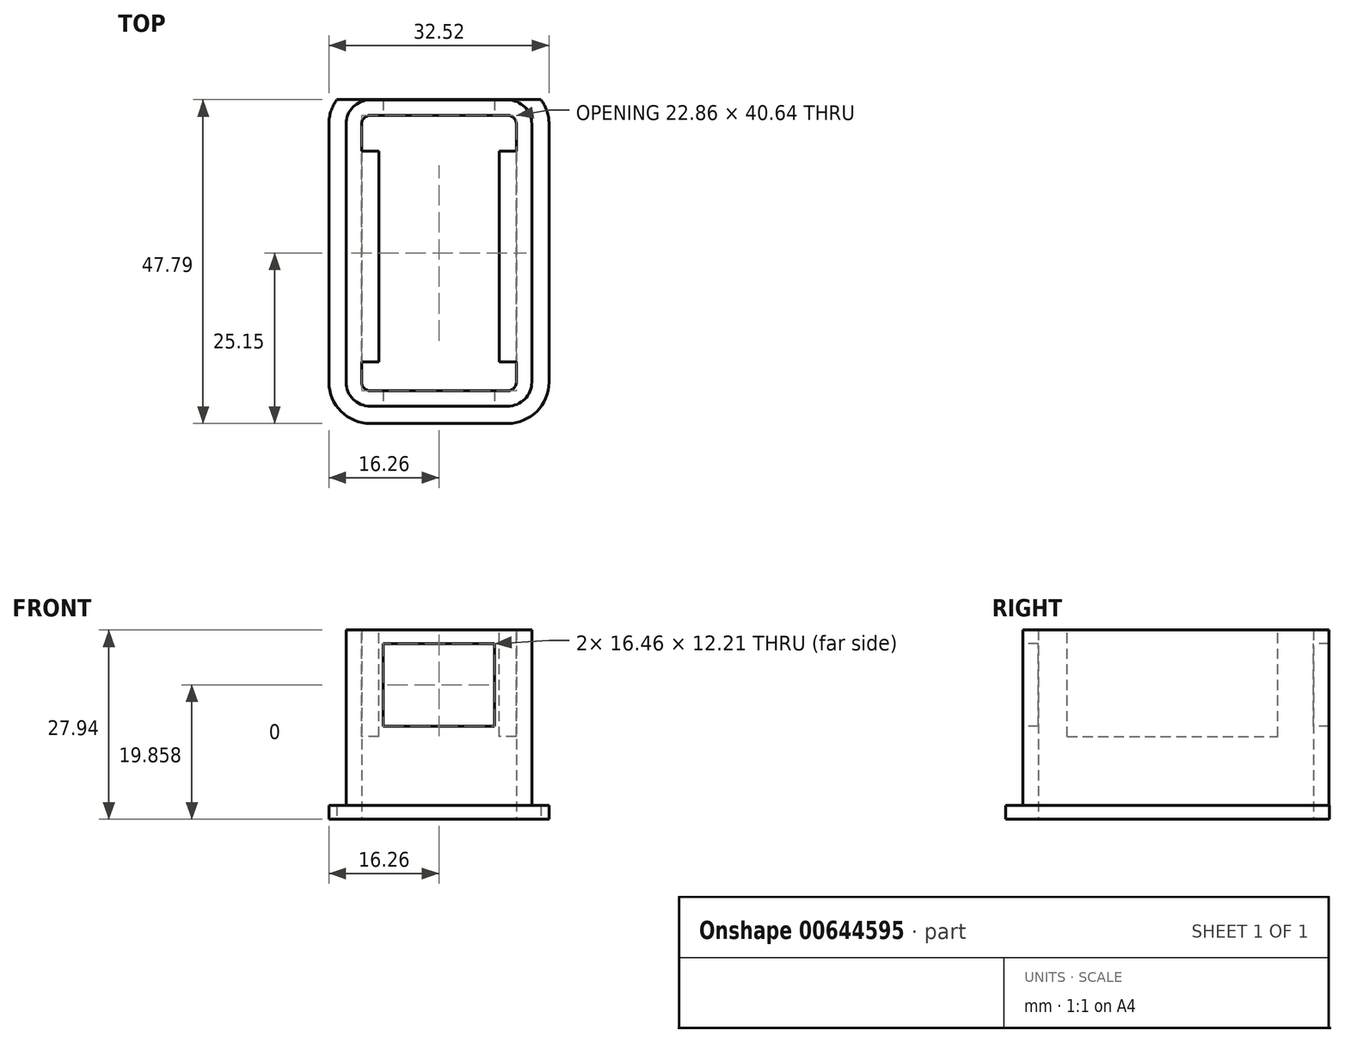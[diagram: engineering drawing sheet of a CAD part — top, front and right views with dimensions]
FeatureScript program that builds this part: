
annotation { "Feature Type Name" : "Feature", "Feature Type Description" : "" }
export const myFeature = defineFeature(function(context is Context, id is Id, definition is map)
    precondition{}
    {
        {
            var Q0;
            Q0=qCreatedBy(makeId("Top.planeOp"),FACE);
            var sketch = newSketch(context, id + "F0", { "sketchPlane" : qUnion([Q0])});
            skLineSegment(sketch, "E0.bottom", {"start": v(1.27, 0) * mm, "end": v(21.59, 0) * mm});
            skLineSegment(sketch, "E0.top", {"start": v(1.27, 40.64) * mm, "end": v(21.59, 40.64) * mm});
            skLineSegment(sketch, "E0.left", {"start": v(0, 1.27) * mm, "end": v(0, 39.37) * mm});
            skLineSegment(sketch, "E0.right", {"start": v(22.86, 1.27) * mm, "end": v(22.86, 39.37) * mm});
            skPoint(sketch, "E1.visualSharp", {"position": v(0, 40.64) * mm});
            skArc(sketch, "E1.filletArc", {"start": v(1.27, 40.64) * mm, "mid": v(0.37, 40.27) * mm, "end": v(0, 39.37) * mm});
            skPoint(sketch, "E2.visualSharp", {"position": v(22.86, 40.64) * mm});
            skArc(sketch, "E2.filletArc", {"start": v(22.86, 39.37) * mm, "mid": v(22.49, 40.27) * mm, "end": v(21.59, 40.64) * mm});
            skPoint(sketch, "E3.visualSharp", {"position": v(22.86, 0) * mm});
            skArc(sketch, "E3.filletArc", {"start": v(21.59, 0) * mm, "mid": v(22.49, 0.37) * mm, "end": v(22.86, 1.27) * mm});
            skPoint(sketch, "E4.visualSharp", {"position": v(0, 0) * mm});
            skArc(sketch, "E4.filletArc", {"start": v(0, 1.27) * mm, "mid": v(0.37, 0.37) * mm, "end": v(1.27, 0) * mm});
            skArc(sketch, "E5.0", {"start": v(-2.29, 1.27) * mm, "mid": v(-1.24, -1.24) * mm, "end": v(1.27, -2.29) * mm});
            skLineSegment(sketch, "E5.1", {"start": v(1.27, -2.29) * mm, "end": v(21.59, -2.29) * mm});
            skLineSegment(sketch, "E5.2", {"start": v(-2.29, 1.27) * mm, "end": v(-2.29, 39.37) * mm});
            skArc(sketch, "E5.3", {"start": v(21.59, -2.29) * mm, "mid": v(24.1, -1.24) * mm, "end": v(25.15, 1.27) * mm});
            skArc(sketch, "E5.4", {"start": v(1.27, 42.93) * mm, "mid": v(-1.24, 41.88) * mm, "end": v(-2.29, 39.37) * mm});
            skLineSegment(sketch, "E5.5", {"start": v(1.27, 42.93) * mm, "end": v(21.59, 42.93) * mm});
            skArc(sketch, "E5.6", {"start": v(25.15, 39.37) * mm, "mid": v(24.1, 41.88) * mm, "end": v(21.59, 42.93) * mm});
            skLineSegment(sketch, "E5.7", {"start": v(25.15, 1.27) * mm, "end": v(25.15, 39.37) * mm});
            skSolve(sketch);
        }
        {
            var Q0;
            Q0=makeQuery(id+"F0.imprint","IMPRINT",FACE,{"disambiguationData":[TD([[makeQuery(id+"F0.imprint","IMPRINT",EDGE,{"derivedFrom":sQuery(id+"F0.wireOp",EDGE,"E0.bottom")}),-1.0]])]});
            extrude(context, id + "F1", {"entities" : qUnion([Q0]), "depth" : 27.94 * mm, "offsetDistance" : 25.4 * mm});
        }
        {
            var Q0;
            Q0=makeQuery(id+"F1.opExtrude","SWEPT_FACE",FACE,{"disambiguationData":[OSD([sQuery(id+"F0.wireOp",EDGE,"E5.1")])]});
            var sketch = newSketch(context, id + "F2", { "sketchPlane" : qUnion([Q0])});
            skLineSegment(sketch, "E6.bottom", {"start": v(3.2, 25.96) * mm, "end": v(19.66, 25.96) * mm});
            skLineSegment(sketch, "E6.top", {"start": v(3.2, 13.75) * mm, "end": v(19.66, 13.75) * mm});
            skLineSegment(sketch, "E6.left", {"start": v(3.2, 25.96) * mm, "end": v(3.2, 13.75) * mm});
            skLineSegment(sketch, "E6.right", {"start": v(19.66, 25.96) * mm, "end": v(19.66, 13.75) * mm});
            skSolve(sketch);
        }
        {
            var Q0;
            Q0=makeQuery(id+"F2.imprint","IMPRINT",FACE,{"disambiguationData":[TD([[makeQuery(id+"F2.imprint","IMPRINT",EDGE,{"derivedFrom":sQuery(id+"F2.wireOp",EDGE,"E6.bottom")}),-1.0]])]});
            extrude(context, id + "F3", {"entities" : qUnion([Q0]), "operationType" : NewBodyOperationType.REMOVE, "oppositeDirection" : true, "depth" : 57.94 * mm, "offsetDistance" : 25.4 * mm});
        }
        {
            var Q0;
            Q0=qCreatedBy(makeId("Top.planeOp"),FACE);
            var sketch = newSketch(context, id + "F4", { "sketchPlane" : qUnion([Q0])});
            skArc(sketch, "E7.0", {"start": v(-3.65, 42.96) * mm, "mid": v(-4.53, 41.26) * mm, "end": v(-4.83, 39.37) * mm});
            skLineSegment(sketch, "E7.1", {"start": v(-4.83, 1.27) * mm, "end": v(-4.83, 39.37) * mm});
            skArc(sketch, "E7.3", {"start": v(-4.83, 1.27) * mm, "mid": v(-3.04, -3.04) * mm, "end": v(1.27, -4.83) * mm});
            skArc(sketch, "E7.4", {"start": v(27.69, 39.37) * mm, "mid": v(27.39, 41.26) * mm, "end": v(26.51, 42.96) * mm});
            skLineSegment(sketch, "E7.5", {"start": v(27.69, 1.27) * mm, "end": v(27.69, 39.37) * mm});
            skArc(sketch, "E7.6", {"start": v(21.59, -4.83) * mm, "mid": v(25.9, -3.04) * mm, "end": v(27.69, 1.27) * mm});
            skLineSegment(sketch, "E7.7", {"start": v(1.27, -4.83) * mm, "end": v(21.59, -4.83) * mm});
            skLineSegment(sketch, "E8", {"start": v(1.03, 42.96) * mm, "end": v(-3.65, 42.96) * mm});
            skLineSegment(sketch, "E9", {"start": v(-3.65, 42.96) * mm, "end": v(26.51, 42.96) * mm});
            skSolve(sketch);
        }
        {
            var Q0;
            {var subQ1=sQuery(id+"F4.wireOp",EDGE,"E7.0");Q0=makeQuery(id+"F4.imprint","IMPRINT",FACE,{"disambiguationData":[TD([[makeQuery(id+"F4.imprint","IMPRINT",EDGE,{"derivedFrom":subQ1}),1.0]])]});}
            extrude(context, id + "F5", {"entities" : qUnion([Q0]), "operationType" : NewBodyOperationType.ADD, "depth" : 2.03 * mm, "offsetDistance" : 25.4 * mm});
        }
        {
            var Q0;
            Q0=makeQuery(id+"F5.boolean.opBoolean","SPLIT",FACE,{"disambiguationData":[TD([makeQuery(id+"F1.opExtrude","SWEPT_FACE",FACE,{"disambiguationData":[OSD([sQuery(id+"F0.wireOp",EDGE,"E0.bottom")])]})])],"derivedFrom":makeQuery(id+"F5.opExtrude","CAP_FACE",FACE,{"disambiguationData":[OSD([sQuery(id+"F4.wireOp",EDGE,"E7.0"),sQuery(id+"F4.wireOp",EDGE,"E7.1"),sQuery(id+"F4.wireOp",EDGE,"E7.3"),sQuery(id+"F4.wireOp",EDGE,"E7.4"),sQuery(id+"F4.wireOp",EDGE,"E7.5"),sQuery(id+"F4.wireOp",EDGE,"E7.6"),sQuery(id+"F4.wireOp",EDGE,"E7.7"),sQuery(id+"F4.wireOp",EDGE,"E9")])],"isStart":false})});
            extrude(context, id + "F6", {"entities" : qUnion([Q0]), "operationType" : NewBodyOperationType.REMOVE, "oppositeDirection" : true, "depth" : 25.4 * mm, "offsetDistance" : 25.4 * mm});
        }
        {
            var Q0;
            Q0=makeQuery(id+"F1.opExtrude","SWEPT_FACE",FACE,{"disambiguationData":[OSD([sQuery(id+"F0.wireOp",EDGE,"E5.2")])]});
            var sketch = newSketch(context, id + "F7", { "sketchPlane" : qUnion([Q0])});
            skLineSegment(sketch, "E10.bottom", {"start": v(-35.37, 12.2) * mm, "end": v(-4.24, 12.2) * mm});
            skLineSegment(sketch, "E10.top", {"start": v(-35.37, 27.94) * mm, "end": v(-4.24, 27.94) * mm});
            skLineSegment(sketch, "E10.left", {"start": v(-35.37, 12.2) * mm, "end": v(-35.37, 27.94) * mm});
            skLineSegment(sketch, "E10.right", {"start": v(-4.24, 12.2) * mm, "end": v(-4.24, 27.94) * mm});
            skPoint(sketch, "E11.start.orphan", {"position": v(-35.59, 0) * mm});
            skSolve(sketch);
        }
        {
            var Q0;
            Q0=makeQuery(id+"F7.imprint","IMPRINT",FACE,{"disambiguationData":[TD([[makeQuery(id+"F7.imprint","IMPRINT",EDGE,{"derivedFrom":sQuery(id+"F7.wireOp",EDGE,"E10.bottom")}),1.0]])]});
            extrude(context, id + "F8", {"entities" : qUnion([Q0]), "operationType" : NewBodyOperationType.ADD, "oppositeDirection" : true, "depth" : 25.4 * mm, "offsetDistance" : 25.4 * mm});
        }
        {
            var Q0;
            Q0=makeQuery(id+"F8.boolean.opBoolean","MERGE",FACE,{"derivedFrom":[makeQuery(id+"F1.opExtrude","CAP_FACE",FACE,{"disambiguationData":[OSD([sQuery(id+"F0.wireOp",EDGE,"E0.bottom"),sQuery(id+"F0.wireOp",EDGE,"E0.top"),sQuery(id+"F0.wireOp",EDGE,"E0.left"),sQuery(id+"F0.wireOp",EDGE,"E0.right"),sQuery(id+"F0.wireOp",EDGE,"E1.filletArc"),sQuery(id+"F0.wireOp",EDGE,"E2.filletArc"),sQuery(id+"F0.wireOp",EDGE,"E3.filletArc"),sQuery(id+"F0.wireOp",EDGE,"E4.filletArc"),sQuery(id+"F0.wireOp",EDGE,"E5.0"),sQuery(id+"F0.wireOp",EDGE,"E5.1"),sQuery(id+"F0.wireOp",EDGE,"E5.2"),sQuery(id+"F0.wireOp",EDGE,"E5.3"),sQuery(id+"F0.wireOp",EDGE,"E5.4"),sQuery(id+"F0.wireOp",EDGE,"E5.5"),sQuery(id+"F0.wireOp",EDGE,"E5.6"),sQuery(id+"F0.wireOp",EDGE,"E5.7")])],"isStart":false}),makeQuery(id+"F8.opExtrude","SWEPT_FACE",FACE,{"disambiguationData":[OSD([sQuery(id+"F7.wireOp",EDGE,"E10.top")])]})]});
            var sketch = newSketch(context, id + "F9", { "sketchPlane" : qUnion([Q0])});
            skLineSegment(sketch, "E12.bottom", {"start": v(2.54, 36.93) * mm, "end": v(20.32, 36.93) * mm});
            skLineSegment(sketch, "E12.top", {"start": v(2.54, 3.91) * mm, "end": v(20.32, 3.91) * mm});
            skLineSegment(sketch, "E12.left", {"start": v(2.54, 36.93) * mm, "end": v(2.54, 3.91) * mm});
            skLineSegment(sketch, "E12.right", {"start": v(20.32, 36.93) * mm, "end": v(20.32, 3.91) * mm});
            skSolve(sketch);
        }
        {
            var Q0;
            {var subQ0=sQuery(id+"F9.wireOp",EDGE,"E12.left");var subQ1=sQuery(id+"F7.wireOp",EDGE,"E10.top");var subQ2=sQuery(id+"F0.wireOp",EDGE,"E5.2");var subQ3=makeQuery(id+"F8.opExtrude","SWEPT_EDGE",EDGE,{"disambiguationData":[OSD([subQ2,subQ1,sQuery(id+"F7.wireOp",EDGE,"E10.left")])]});var subQ4=makeQuery(id+"F9.imprint","INTERSECT",VERTEX,{"derivedFrom":[subQ3,subQ0]});Q0=makeQuery(id+"F9.imprint","IMPRINT",FACE,{"disambiguationData":[TD([[makeQuery(id+"F9.imprint","IMPRINT",EDGE,{"disambiguationData":[TD([[subQ4,-1.0]])],"derivedFrom":subQ0}),1.0]])]});}
            extrude(context, id + "F10", {"entities" : qUnion([Q0]), "operationType" : NewBodyOperationType.REMOVE, "oppositeDirection" : true, "depth" : 42.93 * mm, "offsetDistance" : 25.4 * mm});
        }
    });
